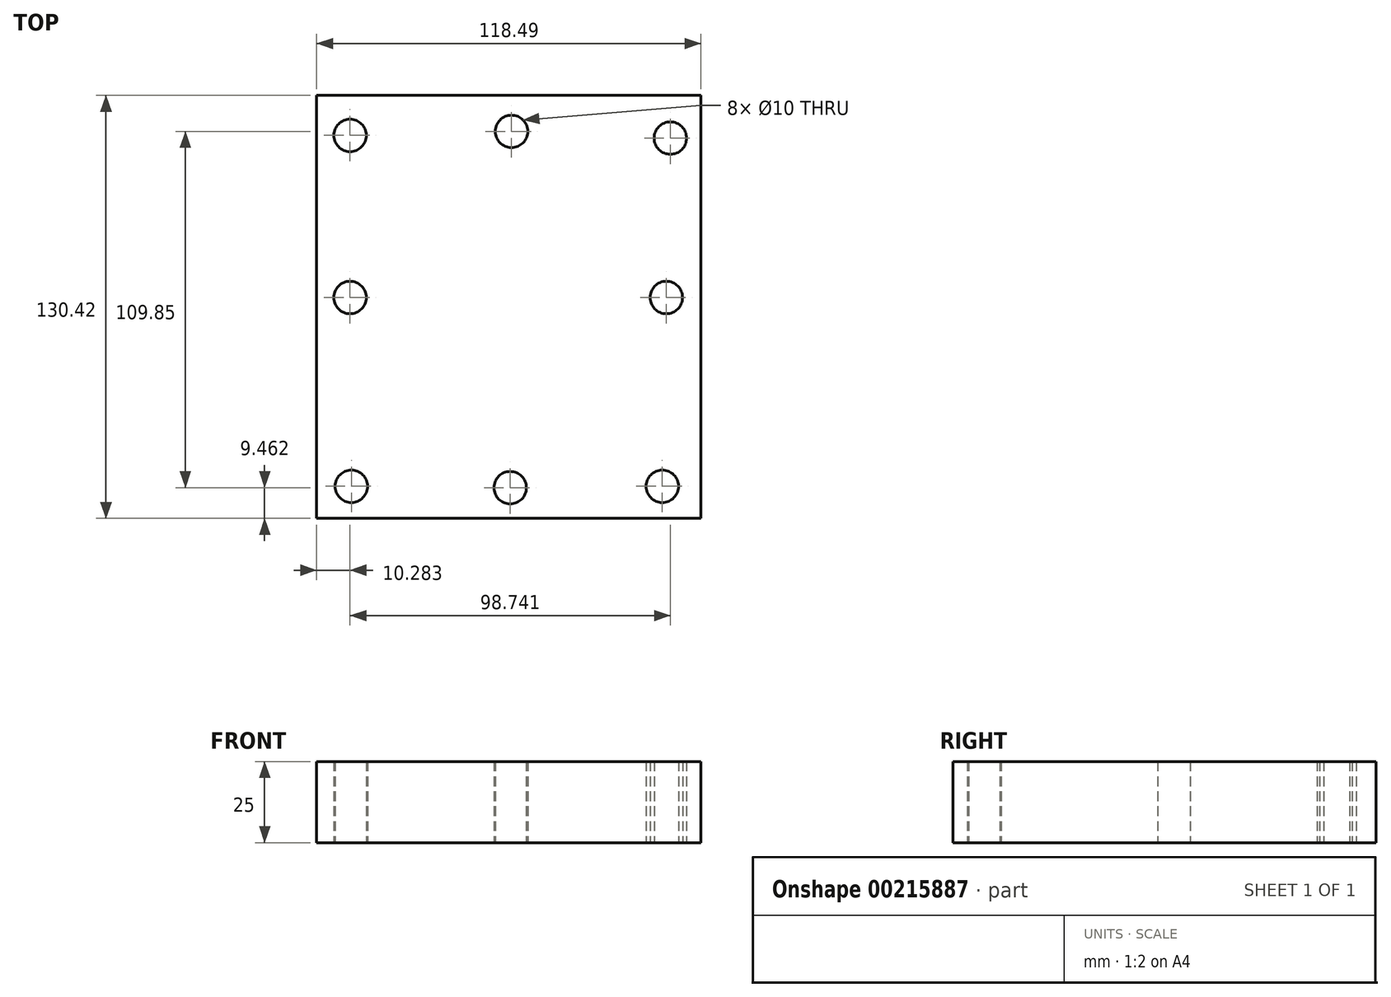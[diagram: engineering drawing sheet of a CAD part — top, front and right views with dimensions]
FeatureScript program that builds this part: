
annotation { "Feature Type Name" : "Feature", "Feature Type Description" : "" }
export const myFeature = defineFeature(function(context is Context, id is Id, definition is map)
    precondition{}
    {
        {
            var Q0;
            Q0=qCreatedBy(makeId("Top.planeOp"),FACE);
            var sketch = newSketch(context, id + "F0", { "sketchPlane" : qUnion([Q0])});
            skLineSegment(sketch, "E0.bottom", {"start": v(-55.54, 62.33) * mm, "end": v(62.95, 62.33) * mm});
            skLineSegment(sketch, "E0.top", {"start": v(-55.54, -68.1) * mm, "end": v(62.95, -68.1) * mm});
            skLineSegment(sketch, "E0.left", {"start": v(-55.54, 62.33) * mm, "end": v(-55.54, -68.1) * mm});
            skLineSegment(sketch, "E0.right", {"start": v(62.95, 62.33) * mm, "end": v(62.95, -68.1) * mm});
            skPoint(sketch, "E1", {"position": v(-45.26, 49.99) * mm});
            skPoint(sketch, "E2", {"position": v(53.48, 49.16) * mm});
            skPoint(sketch, "E3", {"position": v(-44.85, -58.22) * mm});
            skPoint(sketch, "E4", {"position": v(51.02, -58.22) * mm});
            skPoint(sketch, "E5", {"position": v(-45.26, 0) * mm});
            skPoint(sketch, "E6", {"position": v(52.25, 0) * mm});
            skPoint(sketch, "E7", {"position": v(4.53, 51.22) * mm});
            skPoint(sketch, "E8", {"position": v(4.11, -58.63) * mm});
            skPoint(sketch, "E9", {"position": v(23.45, -21.6) * mm});
            skSolve(sketch);
        }
        {
            var Q0;
            Q0=makeQuery(id+"F0.imprint","IMPRINT",FACE,{"disambiguationData":[TD([[makeQuery(id+"F0.imprint","IMPRINT",EDGE,{"derivedFrom":sQuery(id+"F0.wireOp",EDGE,"E0.bottom")}),-1.0]])]});
            extrude(context, id + "F1", {"entities" : qUnion([Q0]), "depth" : 25 * mm});
        }
        {
            var Q0;
            Q0=sQuery(id+"F0.wireOp",VERTEX,"E1");
            var Q1;
            Q1=sQuery(id+"F0.wireOp",VERTEX,"E7");
            var Q2;
            Q2=sQuery(id+"F0.wireOp",VERTEX,"E2");
            var Q3;
            Q3=sQuery(id+"F0.wireOp",VERTEX,"E6");
            var Q4;
            Q4=sQuery(id+"F0.wireOp",VERTEX,"E4");
            var Q5;
            Q5=sQuery(id+"F0.wireOp",VERTEX,"E8");
            var Q6;
            Q6=sQuery(id+"F0.wireOp",VERTEX,"E3");
            var Q7;
            Q7=sQuery(id+"F0.wireOp",VERTEX,"E5");
            var Q8;
            Q8=makeQuery(id+"F1.opExtrude","SWEPT_BODY",BODY,{"disambiguationData":[OSD([sQuery(id+"F0.wireOp",EDGE,"E0.bottom"),sQuery(id+"F0.wireOp",EDGE,"E0.top"),sQuery(id+"F0.wireOp",EDGE,"E0.left"),sQuery(id+"F0.wireOp",EDGE,"E0.right")])]});
            hole(context, id + "F2", {"style" : HoleStyle.SIMPLE, "endStyle" : HoleEndStyle.THROUGH, "oppositeDirection" : true, "holeDiameter" : 10 * mm, "locations" : qUnion([Q0, Q1, Q2, Q3, Q4, Q5, Q6, Q7]), "scope" : qUnion([Q8]), "isTappedThrough" : true});
        }
    });
